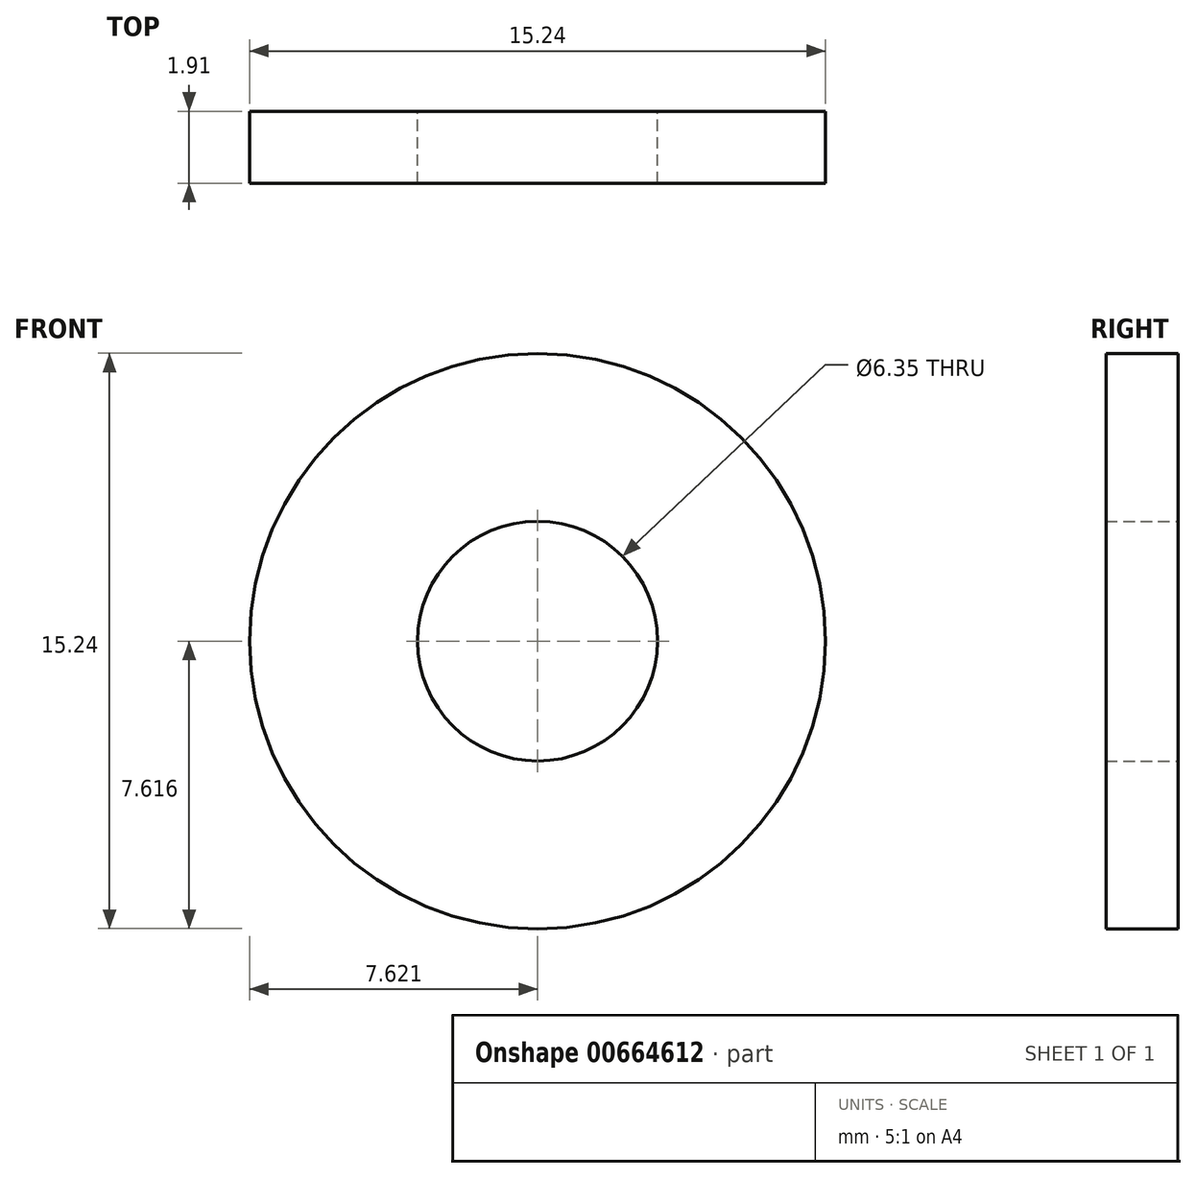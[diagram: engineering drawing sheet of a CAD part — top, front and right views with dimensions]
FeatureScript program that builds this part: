
annotation { "Feature Type Name" : "Feature", "Feature Type Description" : "" }
export const myFeature = defineFeature(function(context is Context, id is Id, definition is map)
    precondition{}
    {
        {
            var Q0;
            Q0=qCreatedBy(makeId("Front.planeOp"),FACE);
            var sketch = newSketch(context, id + "F0", { "sketchPlane" : qUnion([Q0])});
            skCircle(sketch, "E0", {"center": v(-32.17, 19.47) * mm, "radius": 7.62 * mm});
            skCircle(sketch, "E1", {"center": v(-32.17, 19.47) * mm, "radius": 3.18 * mm});
            skSolve(sketch);
        }
        {
            var Q0;
            Q0=makeQuery(id+"F0.imprint","IMPRINT",FACE,{"disambiguationData":[TD([[makeQuery(id+"F0.imprint","IMPRINT",EDGE,{"derivedFrom":sQuery(id+"F0.wireOp",EDGE,"E0")}),1.0]])]});
            extrude(context, id + "F1", {"entities" : qUnion([Q0]), "depth" : 1.9 * mm, "offsetDistance" : 25.4 * mm});
        }
    });
